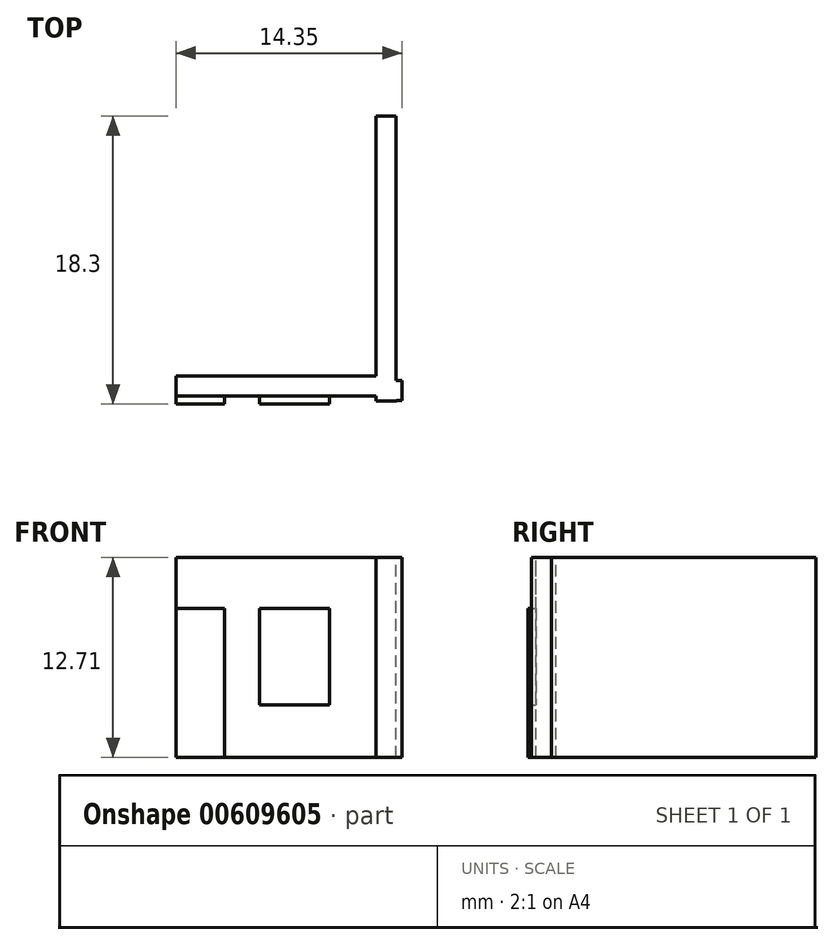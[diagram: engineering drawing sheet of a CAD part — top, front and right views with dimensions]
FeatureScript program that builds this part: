
annotation { "Feature Type Name" : "Feature", "Feature Type Description" : "" }
export const myFeature = defineFeature(function(context is Context, id is Id, definition is map)
    precondition{}
    {
        {
            var Q0;
            Q0=qCreatedBy(makeId("Front.planeOp"),FACE);
            var sketch = newSketch(context, id + "F0", { "sketchPlane" : qUnion([Q0])});
            skLineSegment(sketch, "E0.bottom", {"start": v(0, 0) * mm, "end": v(12.7, 0) * mm});
            skLineSegment(sketch, "E0.top", {"start": v(0, 12.71) * mm, "end": v(12.7, 12.71) * mm});
            skLineSegment(sketch, "E0.left", {"start": v(0, 0) * mm, "end": v(0, 12.71) * mm});
            skLineSegment(sketch, "E0.right", {"start": v(12.7, 0) * mm, "end": v(12.7, 12.71) * mm});
            skSolve(sketch);
        }
        {
            var Q0;
            Q0=qCreatedBy(makeId("Front.planeOp"),FACE);
            var sketch = newSketch(context, id + "F1", { "sketchPlane" : qUnion([Q0])});
            skLineSegment(sketch, "E1.bottom", {"start": v(0, 0) * mm, "end": v(3.08, 0) * mm});
            skLineSegment(sketch, "E1.top", {"start": v(0, 9.46) * mm, "end": v(3.08, 9.46) * mm});
            skLineSegment(sketch, "E1.left", {"start": v(0, 0) * mm, "end": v(0, 9.46) * mm});
            skLineSegment(sketch, "E1.right", {"start": v(3.08, 0) * mm, "end": v(3.08, 9.46) * mm});
            skSolve(sketch);
        }
        {
            var Q0;
            Q0 = qSketchRegion(id + "F1", true);
            extrude(context, id + "F2", {"entities" : qUnion([Q0]), "depth" : 0.5 * mm, "offsetDistance" : 25.4 * mm});
        }
        {
            var Q0;
            Q0 = qSketchRegion(id + "F0", true);
            extrude(context, id + "F3", {"entities" : qUnion([Q0]), "operationType" : NewBodyOperationType.ADD, "oppositeDirection" : true, "depth" : 1.27 * mm, "offsetDistance" : 25.4 * mm});
        }
        {
            var Q0;
            Q0=qCreatedBy(makeId("Front.planeOp"),FACE);
            var sketch = newSketch(context, id + "F4", { "sketchPlane" : qUnion([Q0])});
            skLineSegment(sketch, "E2.bottom", {"start": v(0, 0) * mm, "end": v(2.48, 0) * mm});
            skLineSegment(sketch, "E2.top", {"start": v(0, 8.93) * mm, "end": v(2.48, 8.93) * mm});
            skLineSegment(sketch, "E2.left", {"start": v(0, 0) * mm, "end": v(0, 8.93) * mm});
            skLineSegment(sketch, "E2.right", {"start": v(2.48, 0) * mm, "end": v(2.48, 8.93) * mm});
            skSolve(sketch);
        }
        {
            var Q0;
            Q0 = qSketchRegion(id + "F4", true);
            extrude(context, id + "F5", {"entities" : qUnion([Q0]), "operationType" : NewBodyOperationType.ADD, "oppositeDirection" : true, "depth" : 1.27 * mm, "offsetDistance" : 25.4 * mm});
        }
        {
            var Q0;
            Q0 = qSketchRegion(id + "F4", true);
            extrude(context, id + "F6", {"entities" : qUnion([Q0]), "operationType" : NewBodyOperationType.ADD, "depth" : 0.5 * mm, "offsetDistance" : 25.4 * mm});
        }
        {
            var Q0;
            Q0=qCreatedBy(makeId("Front.planeOp"),FACE);
            var sketch = newSketch(context, id + "F7", { "sketchPlane" : qUnion([Q0])});
            skLineSegment(sketch, "E3.bottom", {"start": v(5.31, 9.47) * mm, "end": v(9.76, 9.47) * mm});
            skLineSegment(sketch, "E3.top", {"start": v(5.31, 3.36) * mm, "end": v(9.76, 3.36) * mm});
            skLineSegment(sketch, "E3.left", {"start": v(5.31, 9.47) * mm, "end": v(5.31, 3.36) * mm});
            skLineSegment(sketch, "E3.right", {"start": v(9.76, 9.47) * mm, "end": v(9.76, 3.36) * mm});
            skSolve(sketch);
        }
        {
            var Q0;
            Q0=makeQuery(id+"F7.imprint","IMPRINT",FACE,{"disambiguationData":[TD([[makeQuery(id+"F7.imprint","IMPRINT",EDGE,{"derivedFrom":sQuery(id+"F7.wireOp",EDGE,"E3.bottom")}),-1.0]])]});
            extrude(context, id + "F8", {"entities" : qUnion([Q0]), "operationType" : NewBodyOperationType.ADD, "depth" : 0.5 * mm, "offsetDistance" : 25.4 * mm});
        }
        {
            var Q0;
            Q0=qCreatedBy(makeId("Front.planeOp"),FACE);
            var sketch = newSketch(context, id + "F9", { "sketchPlane" : qUnion([Q0])});
            skLineSegment(sketch, "E4.bottom", {"start": v(5.67, 9.14) * mm, "end": v(7.27, 9.14) * mm});
            skLineSegment(sketch, "E4.top", {"start": v(5.67, 6.73) * mm, "end": v(7.27, 6.73) * mm});
            skLineSegment(sketch, "E4.left", {"start": v(5.67, 9.14) * mm, "end": v(5.67, 6.73) * mm});
            skLineSegment(sketch, "E4.right", {"start": v(7.27, 9.14) * mm, "end": v(7.27, 6.73) * mm});
            skLineSegment(sketch, "E5.bottom", {"start": v(9.44, 9.15) * mm, "end": v(7.77, 9.15) * mm});
            skLineSegment(sketch, "E5.top", {"start": v(9.44, 6.73) * mm, "end": v(7.77, 6.73) * mm});
            skLineSegment(sketch, "E5.left", {"start": v(9.44, 9.15) * mm, "end": v(9.44, 6.73) * mm});
            skLineSegment(sketch, "E5.right", {"start": v(7.77, 9.15) * mm, "end": v(7.77, 6.73) * mm});
            skLineSegment(sketch, "E6.bottom", {"start": v(5.65, 6.34) * mm, "end": v(7.27, 6.34) * mm});
            skLineSegment(sketch, "E6.top", {"start": v(5.65, 3.76) * mm, "end": v(7.27, 3.76) * mm});
            skLineSegment(sketch, "E6.left", {"start": v(5.65, 6.34) * mm, "end": v(5.65, 3.76) * mm});
            skLineSegment(sketch, "E6.right", {"start": v(7.27, 6.34) * mm, "end": v(7.27, 3.76) * mm});
            skLineSegment(sketch, "E7.bottom", {"start": v(7.77, 6.4) * mm, "end": v(9.44, 6.4) * mm});
            skLineSegment(sketch, "E7.top", {"start": v(7.77, 3.76) * mm, "end": v(9.44, 3.76) * mm});
            skLineSegment(sketch, "E7.left", {"start": v(7.77, 6.4) * mm, "end": v(7.77, 3.76) * mm});
            skLineSegment(sketch, "E7.right", {"start": v(9.44, 6.4) * mm, "end": v(9.44, 3.76) * mm});
            skSolve(sketch);
        }
        {
            var Q0;
            Q0 = qSketchRegion(id + "F9", true);
            extrude(context, id + "F10", {"entities" : qUnion([Q0]), "operationType" : NewBodyOperationType.ADD, "depth" : 0.5 * mm, "offsetDistance" : 25.4 * mm});
        }
        {
            var Q0;
            Q0=qCreatedBy(makeId("Top.planeOp"),FACE);
            var sketch = newSketch(context, id + "F11", { "sketchPlane" : qUnion([Q0])});
            skLineSegment(sketch, "E8.bottom", {"start": v(12.7, -0.32) * mm, "end": v(13.98, -0.32) * mm});
            skLineSegment(sketch, "E8.top", {"start": v(12.7, 17.8) * mm, "end": v(13.98, 17.8) * mm});
            skLineSegment(sketch, "E8.left", {"start": v(12.7, -0.32) * mm, "end": v(12.7, 17.8) * mm});
            skLineSegment(sketch, "E8.right", {"start": v(13.98, -0.32) * mm, "end": v(13.98, 17.8) * mm});
            skSolve(sketch);
        }
        {
            var Q0;
            Q0=qCreatedBy(makeId("Top.planeOp"),FACE);
            var sketch = newSketch(context, id + "F12", { "sketchPlane" : qUnion([Q0])});
            skLineSegment(sketch, "E9.bottom", {"start": v(13.99, -0.3) * mm, "end": v(14.35, -0.3) * mm});
            skLineSegment(sketch, "E9.top", {"start": v(13.99, 1) * mm, "end": v(14.35, 1) * mm});
            skLineSegment(sketch, "E9.left", {"start": v(13.99, -0.3) * mm, "end": v(13.99, 1) * mm});
            skLineSegment(sketch, "E9.right", {"start": v(14.35, -0.3) * mm, "end": v(14.35, 1) * mm});
            skSolve(sketch);
        }
        {
            var Q0;
            Q0=makeQuery(id+"F12.imprint","IMPRINT",FACE,{"disambiguationData":[TD([[makeQuery(id+"F12.imprint","IMPRINT",EDGE,{"derivedFrom":sQuery(id+"F12.wireOp",EDGE,"E9.bottom")}),1.0]])]});
            var Q1;
            Q1 = qSketchRegion(id + "F11", true);
            extrude(context, id + "F13", {"entities" : qUnion([Q0, Q1]), "operationType" : NewBodyOperationType.ADD, "depth" : 12.7 * mm, "offsetDistance" : 25.4 * mm});
        }
    });
